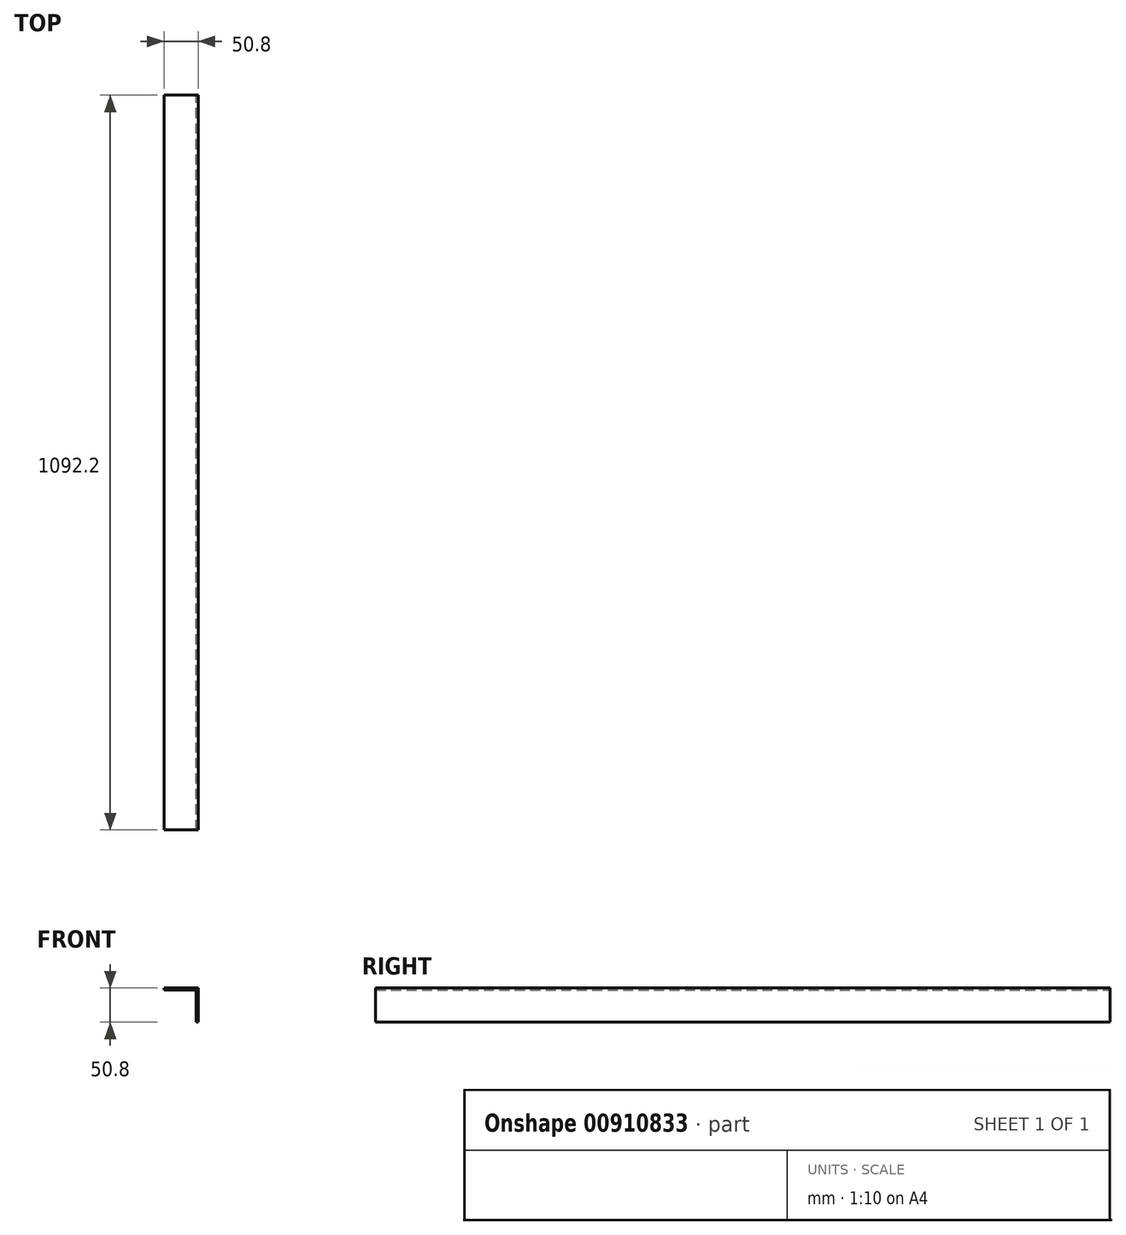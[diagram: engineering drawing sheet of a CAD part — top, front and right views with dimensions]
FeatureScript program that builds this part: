
annotation { "Feature Type Name" : "Feature", "Feature Type Description" : "" }
export const myFeature = defineFeature(function(context is Context, id is Id, definition is map)
    precondition{}
    {
        {
            var Q0;
            Q0=qCreatedBy(makeId("Front.planeOp"),FACE);
            var sketch = newSketch(context, id + "F0", { "sketchPlane" : qUnion([Q0])});
            skLineSegment(sketch, "E0", {"start": v(0, 0) * mm, "end": v(50.8, 0) * mm});
            skLineSegment(sketch, "E1", {"start": v(50.8, 0) * mm, "end": v(50.8, -50.8) * mm});
            skLineSegment(sketch, "E2.0", {"start": v(47.62, -3.18) * mm, "end": v(47.63, -50.8) * mm});
            skLineSegment(sketch, "E2.1", {"start": v(0, -3.18) * mm, "end": v(47.62, -3.18) * mm});
            skLineSegment(sketch, "E3", {"start": v(0, 0) * mm, "end": v(0, -3.18) * mm});
            skLineSegment(sketch, "E4", {"start": v(50.8, -50.8) * mm, "end": v(47.63, -50.8) * mm});
            skSolve(sketch);
        }
        {
            var Q0;
            Q0 = qSketchRegion(id + "F0", true);
            extrude(context, id + "F1", {"entities" : qUnion([Q0]), "flatOperationType" : FlatOperationType.REMOVE, "depth" : 1092.2 * mm, "offsetDistance" : 25.4 * mm, "domain" : OperationDomain.MODEL});
        }
    });
